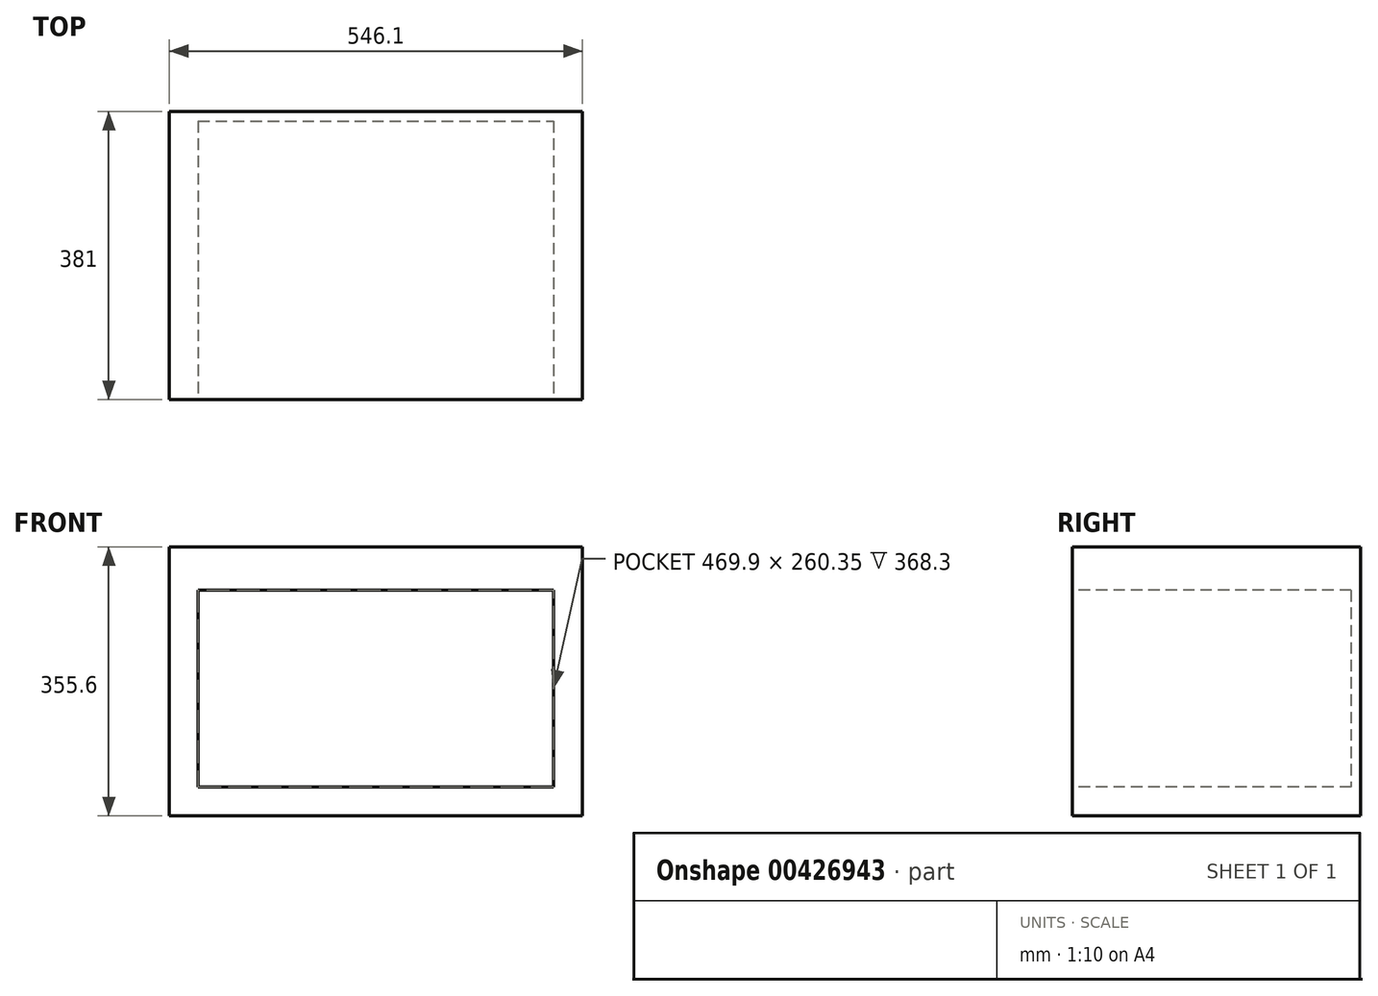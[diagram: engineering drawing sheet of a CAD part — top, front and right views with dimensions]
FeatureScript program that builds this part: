
annotation { "Feature Type Name" : "Feature", "Feature Type Description" : "" }
export const myFeature = defineFeature(function(context is Context, id is Id, definition is map)
    precondition{}
    {
        {
            var Q0;
            Q0=qCreatedBy(makeId("Right.planeOp"),FACE);
            var sketch = newSketch(context, id + "F0", { "sketchPlane" : qUnion([Q0])});
            skLineSegment(sketch, "E0.bottom", {"start": v(0, 0) * mm, "end": v(-381, 0) * mm});
            skLineSegment(sketch, "E0.top", {"start": v(0, 355.6) * mm, "end": v(-381, 355.6) * mm});
            skLineSegment(sketch, "E0.left", {"start": v(0, 0) * mm, "end": v(0, 355.6) * mm});
            skLineSegment(sketch, "E0.right", {"start": v(-381, 0) * mm, "end": v(-381, 355.6) * mm});
            skSolve(sketch);
        }
        {
            var Q0;
            Q0=makeQuery(id+"F0.imprint","IMPRINT",FACE,{"disambiguationData":[TD([[makeQuery(id+"F0.imprint","IMPRINT",EDGE,{"derivedFrom":sQuery(id+"F0.wireOp",EDGE,"E0.bottom")}),-1.0]])]});
            extrude(context, id + "F1", {"entities" : qUnion([Q0]), "depth" : 546.1 * mm});
        }
        {
            var Q0;
            Q0=makeQuery(id+"F1.opExtrude","SWEPT_FACE",FACE,{"disambiguationData":[OSD([sQuery(id+"F0.wireOp",EDGE,"E0.right")])]});
            var sketch = newSketch(context, id + "F2", { "sketchPlane" : qUnion([Q0])});
            skLineSegment(sketch, "E1.bottom", {"start": v(38.1, 298.45) * mm, "end": v(508, 298.45) * mm});
            skLineSegment(sketch, "E1.top", {"start": v(38.1, 38.1) * mm, "end": v(508, 38.1) * mm});
            skLineSegment(sketch, "E1.left", {"start": v(38.1, 298.45) * mm, "end": v(38.1, 38.1) * mm});
            skLineSegment(sketch, "E1.right", {"start": v(508, 298.45) * mm, "end": v(508, 38.1) * mm});
            skSolve(sketch);
        }
        {
            var Q0;
            Q0=makeQuery(id+"F2.imprint","IMPRINT",FACE,{"disambiguationData":[TD([[makeQuery(id+"F2.imprint","IMPRINT",EDGE,{"derivedFrom":sQuery(id+"F2.wireOp",EDGE,"E1.bottom")}),-1.0]])]});
            extrude(context, id + "F3", {"entities" : qUnion([Q0]), "operationType" : NewBodyOperationType.REMOVE, "oppositeDirection" : true, "depth" : 368.3 * mm});
        }
    });
